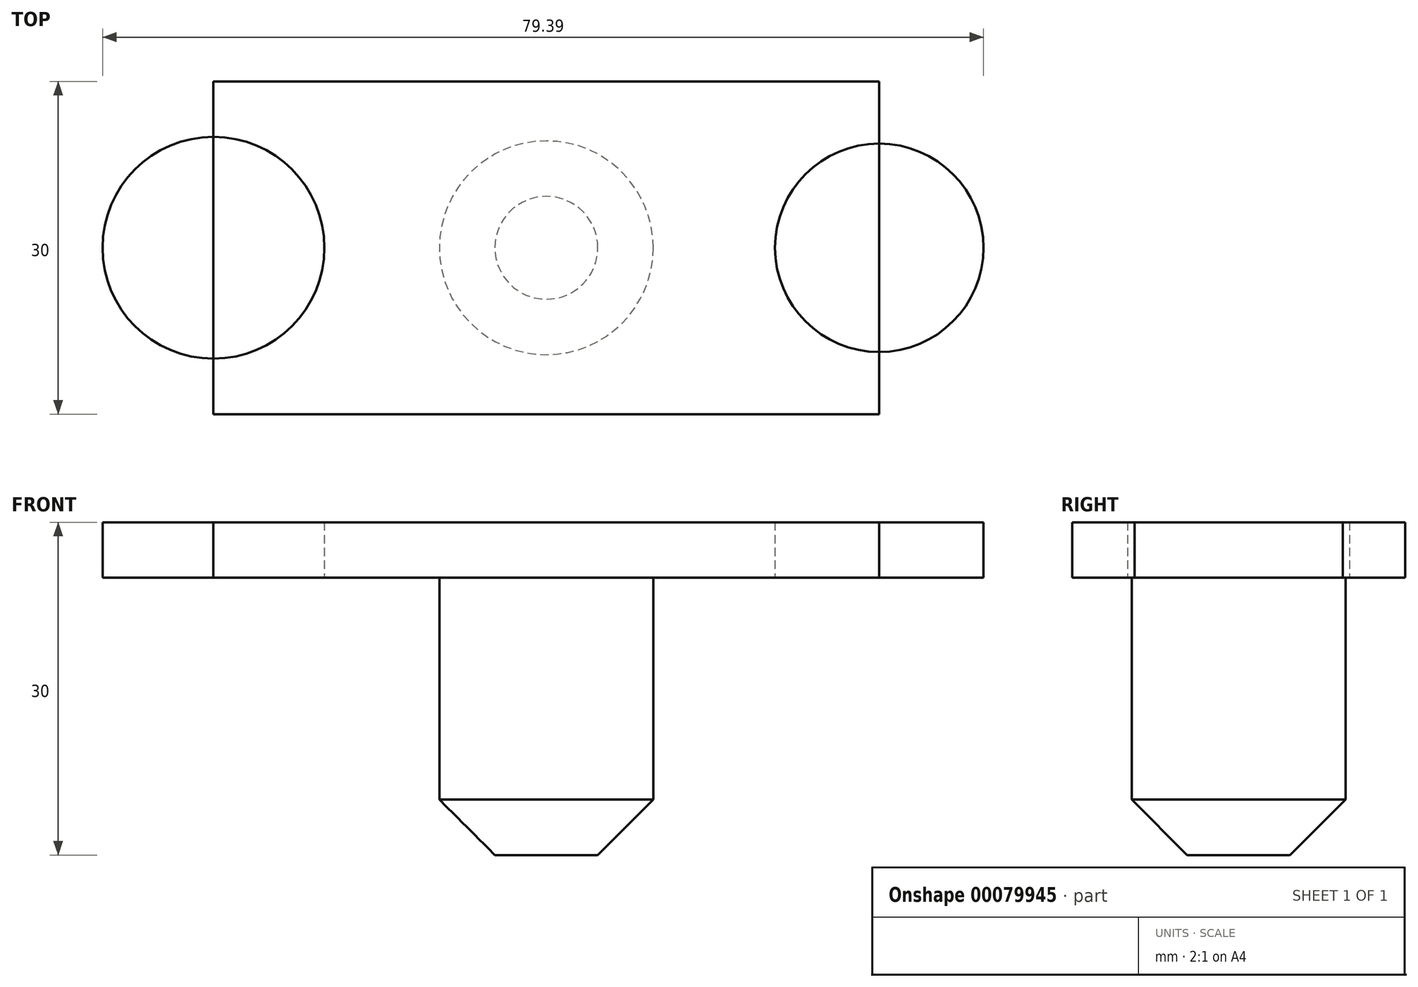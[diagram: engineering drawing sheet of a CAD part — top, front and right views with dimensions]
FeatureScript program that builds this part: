
annotation { "Feature Type Name" : "Feature", "Feature Type Description" : "" }
export const myFeature = defineFeature(function(context is Context, id is Id, definition is map)
    precondition{}
    {
        {
            var Q0;
            Q0=qCreatedBy(makeId("Top.planeOp"),FACE);
            cPlane(context, id + "F0", {"entities" : qUnion([Q0]), "cplaneType" : CPlaneType.OFFSET, "offset" : 152.4 * mm, "width" : 152.4 * mm, "height" : 152.4 * mm});
        }
        {
            var Q0;
            Q0=qCreatedBy(id+"F0.planeOp",FACE);
            var sketch = newSketch(context, id + "F1", { "sketchPlane" : qUnion([Q0])});
            skLineSegment(sketch, "E0.bottom", {"start": v(-30, 15) * mm, "end": v(30, 15) * mm});
            skLineSegment(sketch, "E0.top", {"start": v(-30, -15) * mm, "end": v(30, -15) * mm});
            skLineSegment(sketch, "E0.left", {"start": v(-30, 15) * mm, "end": v(-30, -15) * mm});
            skLineSegment(sketch, "E0.right", {"start": v(30, 15) * mm, "end": v(30, -15) * mm});
            skPoint(sketch, "E0.middle", {"position": v(0, 0) * mm});
            skCircle(sketch, "E1", {"center": v(30, 0) * mm, "radius": 9.4 * mm});
            skCircle(sketch, "E2", {"center": v(-30, 0) * mm, "radius": 10 * mm});
            skSolve(sketch);
        }
        {
            var Q0;
            {var subQ4=sQuery(id+"F1.wireOp",EDGE,"E0.bottom");Q0=makeQuery(id+"F1.imprint","IMPRINT",FACE,{"disambiguationData":[TD([[makeQuery(id+"F1.imprint","IMPRINT",EDGE,{"derivedFrom":subQ4}),-1.0]])]});}
            var Q1;
            {var subQ0=sQuery(id+"F1.wireOp",EDGE,"E2");var subQ1=sQuery(id+"F1.wireOp",EDGE,"E0.left");var subQ2=makeQuery(id+"F1.imprint","INTERSECT",VERTEX,{"disambiguationData":[OD(0.0)],"derivedFrom":[subQ1,subQ0]});Q1=makeQuery(id+"F1.imprint","IMPRINT",FACE,{"disambiguationData":[TD([[makeQuery(id+"F1.imprint","IMPRINT",EDGE,{"disambiguationData":[TD([[subQ2,-1.0]])],"derivedFrom":subQ1}),-1.0]])]});}
            var Q2;
            {var subQ0=sQuery(id+"F1.wireOp",EDGE,"E1");var subQ1=sQuery(id+"F1.wireOp",EDGE,"E0.right");var subQ2=makeQuery(id+"F1.imprint","INTERSECT",VERTEX,{"disambiguationData":[OD(0.0)],"derivedFrom":[subQ1,subQ0]});Q2=makeQuery(id+"F1.imprint","IMPRINT",FACE,{"disambiguationData":[TD([[makeQuery(id+"F1.imprint","IMPRINT",EDGE,{"disambiguationData":[TD([[subQ2,-1.0]])],"derivedFrom":subQ1}),1.0]])]});}
            extrude(context, id + "F2", {"entities" : qUnion([Q0, Q1, Q2]), "depth" : 5 * mm});
        }
        {
            var Q0;
            Q0=makeQuery(id+"F2.opExtrude","CAP_FACE",FACE,{"disambiguationData":[OSD([sQuery(id+"F1.wireOp",EDGE,"E0.bottom"),sQuery(id+"F1.wireOp",EDGE,"E0.top"),sQuery(id+"F1.wireOp",EDGE,"E0.left"),sQuery(id+"F1.wireOp",EDGE,"E0.right"),sQuery(id+"F1.wireOp",EDGE,"E1"),sQuery(id+"F1.wireOp",EDGE,"E2")])],"isStart":true});
            var sketch = newSketch(context, id + "F3", { "sketchPlane" : qUnion([Q0])});
            skCircle(sketch, "E3", {"center": v(0, 0) * mm, "radius": 9.64 * mm});
            skSolve(sketch);
        }
        {
            var Q0;
            Q0=makeQuery(id+"F3.imprint","IMPRINT",FACE,{"disambiguationData":[TD([[makeQuery(id+"F3.imprint","IMPRINT",EDGE,{"derivedFrom":sQuery(id+"F3.wireOp",EDGE,"E3")}),1.0]])]});
            extrude(context, id + "F4", {"entities" : qUnion([Q0]), "operationType" : NewBodyOperationType.ADD, "depth" : 25 * mm});
        }
        {
            var Q0;
            Q0=makeQuery(id+"F4.opExtrude","CAP_EDGE",EDGE,{"disambiguationData":[OSD([sQuery(id+"F3.wireOp",EDGE,"E3")])],"isStart":false});
            chamfer(context, id + "F5", {"entities" : qUnion([Q0]), "width" : 5 * mm, "tangentPropagation" : true});
        }
    });
